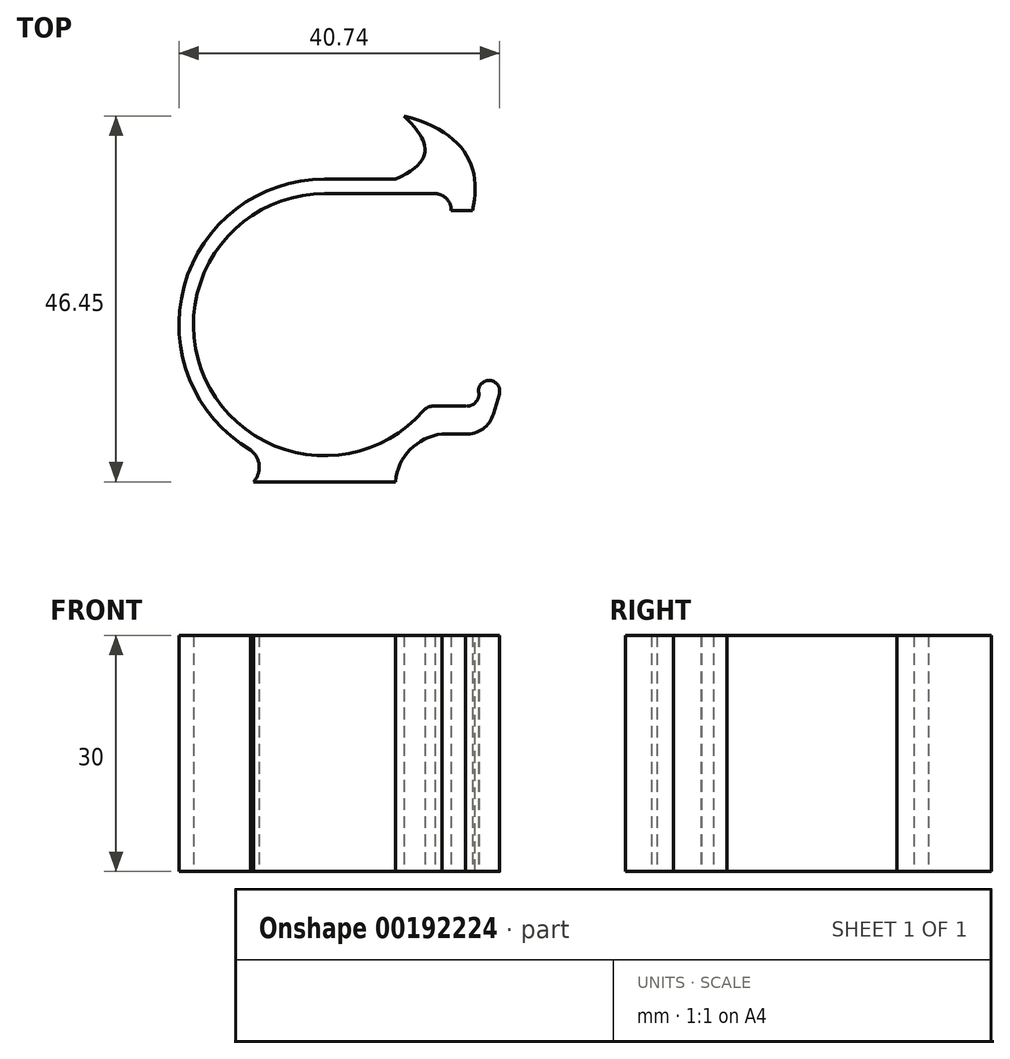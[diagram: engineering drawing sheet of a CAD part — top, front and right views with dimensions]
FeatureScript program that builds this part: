
annotation { "Feature Type Name" : "Feature", "Feature Type Description" : "" }
export const myFeature = defineFeature(function(context is Context, id is Id, definition is map)
    precondition{}
    {
        {
            var Q0;
            Q0=qCreatedBy(makeId("Top.planeOp"),FACE);
            var sketch = newSketch(context, id + "F0", { "sketchPlane" : qUnion([Q0])});
            skArc(sketch, "E0", {"start": v(0, 16.65) * mm, "mid": v(-15, -7.24) * mm, "end": v(13.04, -10.35) * mm});
            skLineSegment(sketch, "E1", {"start": v(-9, -19.95) * mm, "end": v(9, -19.95) * mm});
            skArc(sketch, "E2", {"start": v(13.07, -10.35) * mm, "mid": v(13.05, -10.35) * mm, "end": v(13.04, -10.35) * mm});
            skArc(sketch, "E3", {"start": v(0, 18.5) * mm, "mid": v(-17.85, 4.86) * mm, "end": v(-9.38, -15.94) * mm});
            skPoint(sketch, "E4", {"position": v(-9.38, -15.94) * mm});
            skArc(sketch, "E5", {"start": v(-9, -19.95) * mm, "mid": v(-8.35, -17.6) * mm, "end": v(-9.85, -15.66) * mm});
            skLineSegment(sketch, "E6", {"start": v(0, 16.65) * mm, "end": v(14, 16.65) * mm});
            skLineSegment(sketch, "E7", {"start": v(0, 18.5) * mm, "end": v(9, 18.5) * mm});
            skPoint(sketch, "E8", {"position": v(10.1, 26.5) * mm});
            skFitSpline(sketch, "E9", {"points": [v(10.1, 26.5) * mm, v(18.8, 14.5) * mm], "startDerivative": vector(23.73, -5.94) * mm, "endDerivative": vector(-3.78, -16.08) * mm});
            skFitSpline(sketch, "E10", {"points": [v(10.1, 26.5) * mm, v(9, 18.5) * mm], "startDerivative": vector(7.43, -7.27) * mm, "endDerivative": vector(-18.06, -7.72) * mm});
            skLineSegment(sketch, "E11", {"start": v(16.09, 14.5) * mm, "end": v(18.8, 14.5) * mm});
            skArc(sketch, "E12", {"start": v(14, 16.65) * mm, "mid": v(15.5, 16.02) * mm, "end": v(16.09, 14.5) * mm});
            skArc(sketch, "E13", {"start": v(14.9, -13.89) * mm, "mid": v(10.87, -15.86) * mm, "end": v(9, -19.95) * mm});
            skArc(sketch, "E14", {"start": v(14.04, -10.35) * mm, "mid": v(13.23, -10.46) * mm, "end": v(12.56, -10.93) * mm});
            skLineSegment(sketch, "E15", {"start": v(14.04, -10.35) * mm, "end": v(18.04, -10.35) * mm});
            skLineSegment(sketch, "E16", {"start": v(14.9, -13.89) * mm, "end": v(17.9, -13.89) * mm});
            skArc(sketch, "E17", {"start": v(17.9, -13.89) * mm, "mid": v(20.11, -13.22) * mm, "end": v(21.44, -11.35) * mm});
            skArc(sketch, "E18", {"start": v(17.86, -10.35) * mm, "mid": v(19.09, -9.96) * mm, "end": v(19.61, -8.79) * mm});
            skLineSegment(sketch, "E19", {"start": v(21.44, -11.35) * mm, "end": v(22.19, -8.79) * mm});
            skArc(sketch, "E20", {"start": v(22.19, -8.79) * mm, "mid": v(20.9, -7.07) * mm, "end": v(19.61, -8.79) * mm});
            skSolve(sketch);
        }
        {
            var Q0;
            Q0 = qSketchRegion(id + "F0", true);
            extrude(context, id + "F1", {"entities" : qUnion([Q0]), "endBound" : BoundingType.SYMMETRIC, "depth" : 30 * mm});
        }
    });
